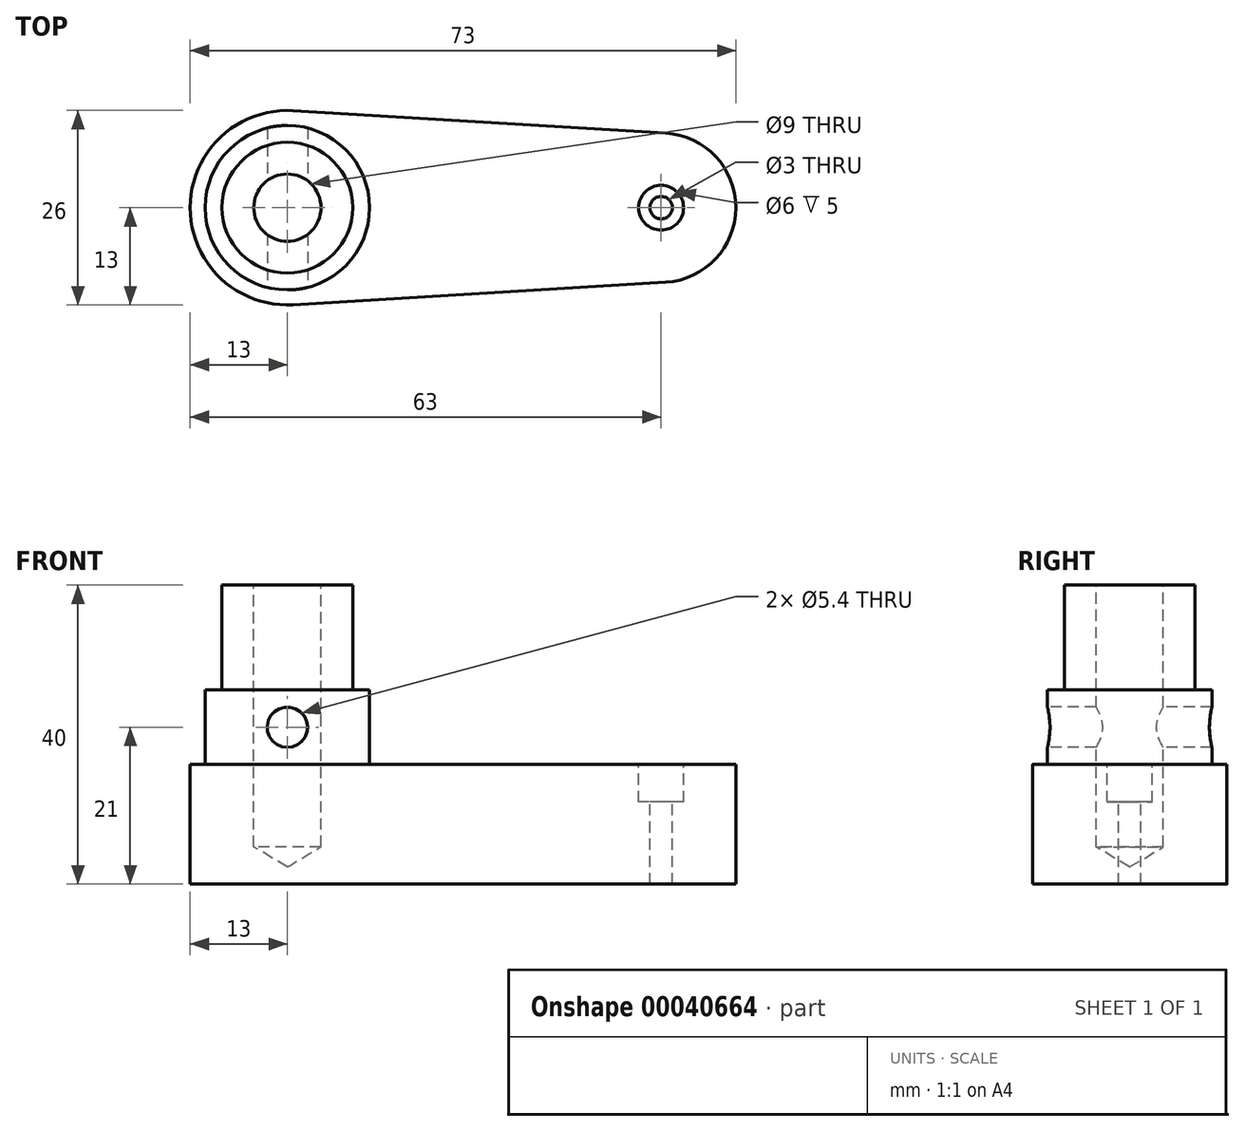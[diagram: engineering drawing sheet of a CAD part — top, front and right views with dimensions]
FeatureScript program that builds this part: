
annotation { "Feature Type Name" : "Feature", "Feature Type Description" : "" }
export const myFeature = defineFeature(function(context is Context, id is Id, definition is map)
    precondition{}
    {
        {
            var Q0;
            Q0=qCreatedBy(makeId("Top.planeOp"),FACE);
            var sketch = newSketch(context, id + "F0", { "sketchPlane" : qUnion([Q0])});
            skLineSegment(sketch, "E0", {"start": v(-11.49, 0) * mm, "end": v(64.24, 0) * mm, "construction": true});
            skLineSegment(sketch, "E1", {"start": v(0, -11.25) * mm, "end": v(0, 30.99) * mm, "construction": true});
            skLineSegment(sketch, "E2", {"start": v(50, -11.57) * mm, "end": v(50, 31.31) * mm, "construction": true});
            skCircle(sketch, "E3", {"center": v(0, 0) * mm, "radius": 13 * mm});
            skCircle(sketch, "E4", {"center": v(50, 0) * mm, "radius": 10 * mm});
            skLineSegment(sketch, "E5", {"start": v(0.78, 12.98) * mm, "end": v(50.6, 9.98) * mm});
            skLineSegment(sketch, "E6", {"start": v(0.78, -12.98) * mm, "end": v(50.6, -9.98) * mm});
            skSolve(sketch);
        }
        {
            var Q0;
            Q0 = qSketchRegion(id + "F0", true);
            extrude(context, id + "F1", {"entities" : qUnion([Q0]), "depth" : 16 * mm});
        }
        {
            var Q0;
            Q0=qCreatedBy(makeId("Top.planeOp"),FACE);
            var sketch = newSketch(context, id + "F2", { "sketchPlane" : qUnion([Q0])});
            skCircle(sketch, "E7", {"center": v(0, 0) * mm, "radius": 11 * mm});
            skSolve(sketch);
        }
        {
            var Q0;
            Q0 = qSketchRegion(id + "F2", true);
            extrude(context, id + "F3", {"entities" : qUnion([Q0]), "operationType" : NewBodyOperationType.ADD, "depth" : 26 * mm});
        }
        {
            var Q0;
            Q0=qCreatedBy(makeId("Top.planeOp"),FACE);
            var sketch = newSketch(context, id + "F4", { "sketchPlane" : qUnion([Q0])});
            skCircle(sketch, "E8", {"center": v(0, 0) * mm, "radius": 8.75 * mm});
            skSolve(sketch);
        }
        {
            var Q0;
            Q0 = qSketchRegion(id + "F4", true);
            extrude(context, id + "F5", {"entities" : qUnion([Q0]), "operationType" : NewBodyOperationType.ADD, "depth" : 40 * mm});
        }
        {
            var Q0;
            Q0=makeQuery(id+"F5.opExtrude","CAP_FACE",FACE,{"disambiguationData":[OSD([sQuery(id+"F4.wireOp",EDGE,"E8")])],"isStart":false});
            var sketch = newSketch(context, id + "F6", { "sketchPlane" : qUnion([Q0])});
            skLineSegment(sketch, "E9", {"start": v(0, 0) * mm, "end": v(26.1, 0) * mm, "construction": true});
            skLineSegment(sketch, "E10", {"start": v(0, 0) * mm, "end": v(0, 20.1) * mm, "construction": true});
            skSolve(sketch);
        }
        {
            var Q0;
            Q0=sQuery(id+"F6.wireOp",VERTEX,"E9.start");
            var Q1;
            Q1=makeQuery(id+"F1.opExtrude","SWEPT_BODY",BODY,{"disambiguationData":[OSD([sQuery(id+"F0.wireOp",EDGE,"E3"),sQuery(id+"F0.wireOp",EDGE,"E4"),sQuery(id+"F0.wireOp",EDGE,"E5"),sQuery(id+"F0.wireOp",EDGE,"E6")])]});
            hole(context, id + "F7", {"style" : HoleStyle.SIMPLE, "holeDiameter" : 9 * mm, "endStyle" : HoleEndStyle.BLIND, "holeDepth" : 35 * mm, "locations" : qUnion([Q0]), "scope" : qUnion([Q1])});
        }
        {
            var Q0;
            Q0=qCreatedBy(makeId("Front.planeOp"),FACE);
            var sketch = newSketch(context, id + "F8", { "sketchPlane" : qUnion([Q0])});
            skLineSegment(sketch, "E11", {"start": v(0, 0) * mm, "end": v(0, 72.33) * mm, "construction": true});
            skLineSegment(sketch, "E12", {"start": v(-25.51, 21) * mm, "end": v(23.96, 21) * mm, "construction": true});
            skCircle(sketch, "E13", {"center": v(0, 21) * mm, "radius": 2.7 * mm});
            skSolve(sketch);
        }
        {
            var Q0;
            Q0 = qSketchRegion(id + "F8", true);
            extrude(context, id + "F9", {"entities" : qUnion([Q0]), "operationType" : NewBodyOperationType.REMOVE, "endBound" : BoundingType.SYMMETRIC, "oppositeDirection" : true, "depth" : 25 * mm});
        }
        {
            var Q0;
            Q0=makeQuery(id+"F1.opExtrude","CAP_FACE",FACE,{"disambiguationData":[OSD([sQuery(id+"F0.wireOp",EDGE,"E3"),sQuery(id+"F0.wireOp",EDGE,"E4"),sQuery(id+"F0.wireOp",EDGE,"E5"),sQuery(id+"F0.wireOp",EDGE,"E6")])],"isStart":false});
            var sketch = newSketch(context, id + "F10", { "sketchPlane" : qUnion([Q0])});
            skLineSegment(sketch, "E14", {"start": v(50, 0) * mm, "end": v(73.03, 0) * mm, "construction": true});
            skPoint(sketch, "E14.endSnap0", {"position": v(60, 0) * mm});
            skLineSegment(sketch, "E15", {"start": v(50, 0) * mm, "end": v(50, 27.13) * mm, "construction": true});
            skSolve(sketch);
        }
        {
            var Q0;
            Q0=sQuery(id+"F10.wireOp",VERTEX,"E15.start");
            var Q1;
            Q1=makeQuery(id+"F1.opExtrude","SWEPT_BODY",BODY,{"disambiguationData":[OSD([sQuery(id+"F0.wireOp",EDGE,"E3"),sQuery(id+"F0.wireOp",EDGE,"E4"),sQuery(id+"F0.wireOp",EDGE,"E5"),sQuery(id+"F0.wireOp",EDGE,"E6")])]});
            hole(context, id + "F11", {"style" : HoleStyle.C_BORE, "holeDiameter" : 3 * mm, "cBoreDiameter" : 6 * mm, "cBoreDepth" : 5 * mm, "endStyle" : HoleEndStyle.THROUGH, "locations" : qUnion([Q0]), "scope" : qUnion([Q1])});
        }
    });
